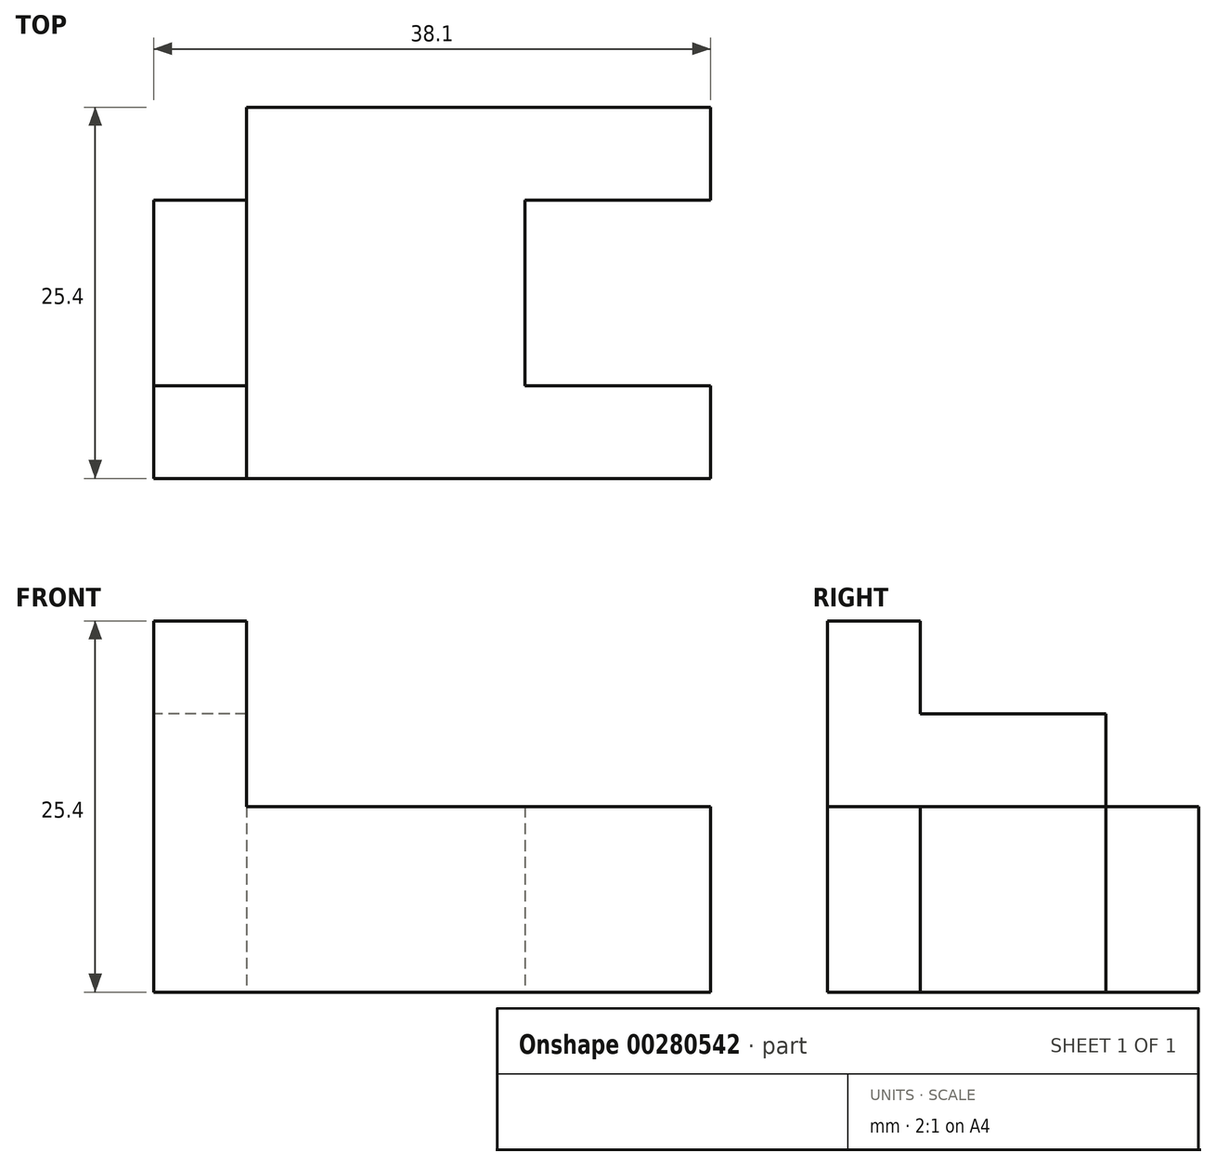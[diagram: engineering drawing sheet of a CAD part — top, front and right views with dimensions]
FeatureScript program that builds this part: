
annotation { "Feature Type Name" : "Feature", "Feature Type Description" : "" }
export const myFeature = defineFeature(function(context is Context, id is Id, definition is map)
    precondition{}
    {
        {
            var Q0;
            Q0=qCreatedBy(makeId("Top.planeOp"),FACE);
            var sketch = newSketch(context, id + "F0", { "sketchPlane" : qUnion([Q0])});
            skLineSegment(sketch, "E0", {"start": v(0, 0) * mm, "end": v(38.1, 0) * mm});
            skLineSegment(sketch, "E1", {"start": v(38.1, 0) * mm, "end": v(38.1, 6.35) * mm});
            skLineSegment(sketch, "E2", {"start": v(38.1, 6.35) * mm, "end": v(25.4, 6.35) * mm});
            skLineSegment(sketch, "E3", {"start": v(25.4, 6.35) * mm, "end": v(25.4, 19.05) * mm});
            skLineSegment(sketch, "E4", {"start": v(25.4, 19.05) * mm, "end": v(38.1, 19.05) * mm});
            skLineSegment(sketch, "E5", {"start": v(38.1, 19.05) * mm, "end": v(38.1, 25.4) * mm});
            skLineSegment(sketch, "E6", {"start": v(38.1, 25.4) * mm, "end": v(0, 25.4) * mm});
            skLineSegment(sketch, "E7", {"start": v(0, 6.35) * mm, "end": v(0, 19.05) * mm});
            skLineSegment(sketch, "E8", {"start": v(0, 25.4) * mm, "end": v(6.35, 25.4) * mm});
            skLineSegment(sketch, "E9", {"start": v(6.35, 25.4) * mm, "end": v(6.35, 0) * mm});
            skLineSegment(sketch, "E10", {"start": v(0, 25.4) * mm, "end": v(0, 19.05) * mm});
            skLineSegment(sketch, "E11", {"start": v(6.35, 19.05) * mm, "end": v(0, 19.05) * mm});
            skLineSegment(sketch, "E12", {"start": v(0, 6.35) * mm, "end": v(0, 0) * mm});
            skLineSegment(sketch, "E13", {"start": v(0, 6.35) * mm, "end": v(6.35, 6.35) * mm});
            skSolve(sketch);
        }
        {
            var Q0;
            {var subQ3=sQuery(id+"F0.wireOp",EDGE,"E1");Q0=makeQuery(id+"F0.imprint","IMPRINT",FACE,{"disambiguationData":[TD([[makeQuery(id+"F0.imprint","IMPRINT",EDGE,{"derivedFrom":subQ3}),1.0]])]});}
            extrude(context, id + "F1", {"entities" : qUnion([Q0]), "depth" : 12.7 * mm});
        }
        {
            var Q0;
            Q0=makeQuery(id+"F0.imprint","IMPRINT",FACE,{"disambiguationData":[TD([[makeQuery(id+"F0.imprint","IMPRINT",EDGE,{"derivedFrom":sQuery(id+"F0.wireOp",EDGE,"E7")}),-1.0]])]});
            extrude(context, id + "F2", {"entities" : qUnion([Q0]), "operationType" : NewBodyOperationType.ADD, "depth" : 19.05 * mm});
        }
        {
            var Q0;
            {var subQ0=sQuery(id+"F0.wireOp",EDGE,"E12");Q0=makeQuery(id+"F0.imprint","IMPRINT",FACE,{"disambiguationData":[TD([[makeQuery(id+"F0.imprint","IMPRINT",EDGE,{"derivedFrom":subQ0}),1.0]])]});}
            var Q1;
            {var subQ0=sQuery(id+"F0.wireOp",EDGE,"E8");Q1=makeQuery(id+"F0.imprint","IMPRINT",FACE,{"disambiguationData":[TD([[makeQuery(id+"F0.imprint","IMPRINT",EDGE,{"derivedFrom":subQ0}),-1.0]])]});}
            extrude(context, id + "F3", {"entities" : qUnion([Q0, Q1]), "operationType" : NewBodyOperationType.ADD, "depth" : 25.4 * mm});
        }
    });
